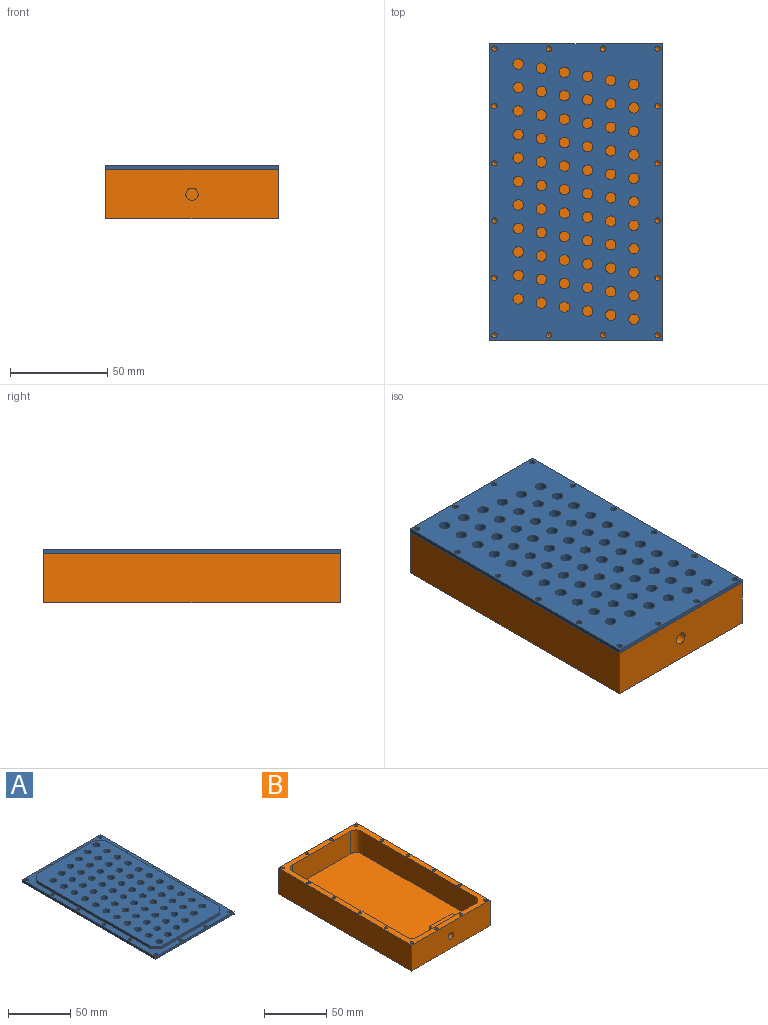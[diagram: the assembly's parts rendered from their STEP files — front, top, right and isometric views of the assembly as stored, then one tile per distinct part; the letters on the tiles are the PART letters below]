
ASSEMBLY  parts=2 mates=1
PART A: 97 faces, bbox 88.9x152.4x4.8 mm
  f0: cylinder r=1.39mm len=2.78mm, axis (0,0,1), area 20mm2, adj f19,f90
  f1: cylinder r=1.39mm len=2.78mm, axis (0,0,1), area 20mm2, adj f19,f90
  f2: cylinder r=1.39mm len=2.78mm, axis (0,0,1), area 20mm2, adj f19,f90
  f3: cylinder r=1.39mm len=2.78mm, axis (0,0,1), area 20mm2, adj f19,f90
  f4: cylinder r=1.39mm len=2.78mm, axis (0,0,1), area 20mm2, adj f19,f90
  f5: cylinder r=1.39mm len=2.78mm, axis (0,0,1), area 20mm2, adj f19,f90
  f6: cylinder r=1.39mm len=2.78mm, axis (0,0,1), area 20mm2, adj f19,f90
  f7: cylinder r=1.39mm len=2.78mm, axis (0,0,1), area 20mm2, adj f19,f90
  f8: cylinder r=1.39mm len=2.78mm, axis (0,0,1), area 20mm2, adj f19,f90
  f9: cylinder r=1.39mm len=2.78mm, axis (0,0,1), area 20mm2, adj f19,f90
  f10: cylinder r=1.39mm len=2.78mm, axis (0,0,1), area 20mm2, adj f19,f90
  f11: cylinder r=1.39mm len=2.78mm, axis (0,0,1), area 20mm2, adj f19,f90
  f12: cylinder r=1.39mm len=2.78mm, axis (0,0,1), area 20mm2, adj f19,f90
  f13: cylinder r=1.39mm len=2.78mm, axis (0,0,1), area 20mm2, adj f19,f90
  f14: plane 152.4x2.29mm, normal (1,0,0), area 348.4mm2, adj f17,f18,f19,f90
  f15: plane 142.24x78.74mm, normal (0,0,1), area 9602.1mm2, adj f20,f21,f22,f23,f24,f25,f26,f27
  f16: plane 152.4x2.29mm, normal (-1,0,0), area 348.4mm2, adj f17,f18,f19,f90
  f17: plane 88.9x2.29mm, normal (0,-1,0), area 203.2mm2, adj f14,f16,f19,f90
  f18: plane 88.9x2.29mm, normal (0,1,0), area 203.2mm2, adj f14,f16,f19,f90
  f19: plane 152.4x88.9mm, normal (0,0,-1), area 11934.1mm2, adj f0,f1,f2,f3,f4,f5,f6,f7
  f20: cylinder r=2.71mm len=5.41mm, axis (0,0,-1), area 82mm2, adj f15,f19
  f21: cylinder r=2.71mm len=5.41mm, axis (0,0,-1), area 82mm2, adj f15,f19
  f22: cylinder r=2.71mm len=5.41mm, axis (0,0,-1), area 82mm2, adj f15,f19
  f23: cylinder r=2.71mm len=5.41mm, axis (0,0,-1), area 82mm2, adj f15,f19
  f24: cylinder r=2.71mm len=5.41mm, axis (0,0,-1), area 82mm2, adj f15,f19
  f25: cylinder r=2.71mm len=5.41mm, axis (0,0,-1), area 82mm2, adj f15,f19
  f26: cylinder r=2.71mm len=5.41mm, axis (0,0,-1), area 82mm2, adj f15,f19
  f27: cylinder r=2.71mm len=5.41mm, axis (0,0,-1), area 82mm2, adj f15,f19
  f28: cylinder r=2.71mm len=5.41mm, axis (0,0,-1), area 82mm2, adj f15,f19
  f29: cylinder r=2.71mm len=5.41mm, axis (0,0,-1), area 82mm2, adj f15,f19
  f30: cylinder r=2.71mm len=5.41mm, axis (0,0,-1), area 82mm2, adj f15,f19
  f31: cylinder r=2.71mm len=5.41mm, axis (0,0,-1), area 82mm2, adj f15,f19
  f32: cylinder r=2.71mm len=5.41mm, axis (0,0,-1), area 82mm2, adj f15,f19
  f33: cylinder r=2.71mm len=5.41mm, axis (0,0,-1), area 82mm2, adj f15,f19
  f34: cylinder r=2.71mm len=5.41mm, axis (0,0,-1), area 82mm2, adj f15,f19
  f35: cylinder r=2.71mm len=5.41mm, axis (0,0,-1), area 82mm2, adj f15,f19
  f36: cylinder r=2.71mm len=5.41mm, axis (0,0,-1), area 82mm2, adj f15,f19
  f37: cylinder r=2.71mm len=5.41mm, axis (0,0,-1), area 82mm2, adj f15,f19
  f38: cylinder r=2.71mm len=5.41mm, axis (0,0,-1), area 82mm2, adj f15,f19
  f39: cylinder r=2.71mm len=5.41mm, axis (0,0,-1), area 82mm2, adj f15,f19
  f40: cylinder r=2.71mm len=5.41mm, axis (0,0,-1), area 82mm2, adj f15,f19
  f41: cylinder r=2.71mm len=5.41mm, axis (0,0,-1), area 82mm2, adj f15,f19
  f42: cylinder r=2.71mm len=5.41mm, axis (0,0,-1), area 82mm2, adj f15,f19
  f43: cylinder r=2.71mm len=5.41mm, axis (0,0,-1), area 82mm2, adj f15,f19
  f44: cylinder r=2.71mm len=5.41mm, axis (0,0,-1), area 82mm2, adj f15,f19
  f45: cylinder r=2.71mm len=5.41mm, axis (0,0,-1), area 82mm2, adj f15,f19
  f46: cylinder r=2.71mm len=5.41mm, axis (0,0,-1), area 82mm2, adj f15,f19
  f47: cylinder r=2.71mm len=5.41mm, axis (0,0,-1), area 82mm2, adj f15,f19
  f48: cylinder r=2.71mm len=5.41mm, axis (0,0,-1), area 82mm2, adj f15,f19
  f49: cylinder r=2.71mm len=5.41mm, axis (0,0,-1), area 82mm2, adj f15,f19
  f50: cylinder r=2.71mm len=5.41mm, axis (0,0,-1), area 82mm2, adj f15,f19
  f51: cylinder r=2.71mm len=5.41mm, axis (0,0,-1), area 82mm2, adj f15,f19
  f52: cylinder r=2.71mm len=5.41mm, axis (0,0,-1), area 82mm2, adj f15,f19
  f53: cylinder r=2.71mm len=5.41mm, axis (0,0,-1), area 82mm2, adj f15,f19
  f54: cylinder r=2.71mm len=5.41mm, axis (0,0,-1), area 82mm2, adj f15,f19
  f55: cylinder r=2.71mm len=5.41mm, axis (0,0,-1), area 82mm2, adj f15,f19
  f56: cylinder r=2.71mm len=5.41mm, axis (0,0,-1), area 82mm2, adj f15,f19
  f57: cylinder r=2.71mm len=5.41mm, axis (0,0,-1), area 82mm2, adj f15,f19
  f58: cylinder r=2.71mm len=5.41mm, axis (0,0,-1), area 82mm2, adj f15,f19
  f59: cylinder r=2.71mm len=5.41mm, axis (0,0,-1), area 82mm2, adj f15,f19
  f60: cylinder r=2.71mm len=5.41mm, axis (0,0,-1), area 82mm2, adj f15,f19
  f61: cylinder r=2.71mm len=5.41mm, axis (0,0,-1), area 82mm2, adj f15,f19
  f62: cylinder r=2.71mm len=5.41mm, axis (0,0,-1), area 82mm2, adj f15,f19
  f63: cylinder r=2.71mm len=5.41mm, axis (0,0,-1), area 82mm2, adj f15,f19
  f64: cylinder r=2.71mm len=5.41mm, axis (0,0,-1), area 82mm2, adj f15,f19
  f65: cylinder r=2.71mm len=5.41mm, axis (0,0,-1), area 82mm2, adj f15,f19
  f66: cylinder r=2.71mm len=5.41mm, axis (0,0,-1), area 82mm2, adj f15,f19
  f67: cylinder r=2.71mm len=5.41mm, axis (0,0,-1), area 82mm2, adj f15,f19
  f68: cylinder r=2.71mm len=5.41mm, axis (0,0,-1), area 82mm2, adj f15,f19
  f69: cylinder r=2.71mm len=5.41mm, axis (0,0,-1), area 82mm2, adj f15,f19
  f70: cylinder r=2.71mm len=5.41mm, axis (0,0,-1), area 82mm2, adj f15,f19
  f71: cylinder r=2.71mm len=5.41mm, axis (0,0,-1), area 82mm2, adj f15,f19
  f72: cylinder r=2.71mm len=5.41mm, axis (0,0,-1), area 82mm2, adj f15,f19
  f73: cylinder r=2.71mm len=5.41mm, axis (0,0,-1), area 82mm2, adj f15,f19
  f74: cylinder r=2.71mm len=5.41mm, axis (0,0,-1), area 82mm2, adj f15,f19
  f75: cylinder r=2.71mm len=5.41mm, axis (0,0,-1), area 82mm2, adj f15,f19
  f76: cylinder r=2.71mm len=5.41mm, axis (0,0,-1), area 82mm2, adj f15,f19
  f77: cylinder r=2.71mm len=5.41mm, axis (0,0,-1), area 82mm2, adj f15,f19
  f78: cylinder r=2.71mm len=5.41mm, axis (0,0,-1), area 82mm2, adj f15,f19
  f79: cylinder r=2.71mm len=5.41mm, axis (0,0,-1), area 82mm2, adj f15,f19
  f80: cylinder r=2.71mm len=5.41mm, axis (0,0,-1), area 82mm2, adj f15,f19
  f81: cylinder r=2.71mm len=5.41mm, axis (0,0,-1), area 82mm2, adj f15,f19
  f82: cylinder r=2.71mm len=5.41mm, axis (0,0,-1), area 82mm2, adj f15,f19
  f83: cylinder r=2.71mm len=5.41mm, axis (0,0,-1), area 82mm2, adj f15,f19
  f84: cylinder r=2.71mm len=5.41mm, axis (0,0,-1), area 82mm2, adj f15,f19
  f85: cylinder r=2.71mm len=5.41mm, axis (0,0,-1), area 82mm2, adj f15,f19
  f86: plane 129.54x2.54mm, normal (-1,0,0), area 329mm2, adj f15,f90,f91,f94
  f87: plane 66.04x2.54mm, normal (0,1,0), area 167.7mm2, adj f15,f90,f91,f92
  f88: plane 129.54x2.54mm, normal (1,0,0), area 329mm2, adj f15,f90,f92,f93
  f89: plane 66.04x2.54mm, normal (0,-1,0), area 167.7mm2, adj f15,f90,f93,f94
  f90: plane 152.4x88.9mm, normal (0,0,1), area 2332mm2, adj f0,f1,f2,f3,f4,f5,f6,f7
  f91: plane 6.35x6.35mm, normal (-0.71,0.71,0), area 22.8mm2, adj f15,f86,f87,f90
  f92: plane 6.35x6.35mm, normal (0.71,0.71,0), area 22.8mm2, adj f15,f87,f88,f90
  f93: plane 6.35x6.35mm, normal (0.71,-0.71,0), area 22.8mm2, adj f15,f88,f89,f90
  f94: plane 6.35x6.35mm, normal (-0.71,-0.71,0), area 22.8mm2, adj f15,f86,f89,f90
  f95: cylinder r=1.39mm len=2.78mm, axis (0,0,1), area 20mm2, adj f19,f90
  f96: cylinder r=1.39mm len=2.78mm, axis (0,0,1), area 20mm2, adj f19,f90
PART B: 64 faces, bbox 88.9x152.4x25.4 mm
  f0: plane 25.4x19.18mm, normal (0,1,0), area 455.4mm2, adj f1,f2,f27,f62,f63
  f1: cylinder r=6.35mm len=19.18mm, axis (0,0,1), area 191.3mm2, adj f0,f23,f27,f63
  f2: cylinder r=6.35mm len=19.18mm, axis (0,0,-1), area 191.3mm2, adj f0,f23,f27,f63
  f3: cone r=0mm half-angle=59deg, axis (0,0,1), area 6.7mm2, adj f4
  f4: cylinder r=1.35mm len=11.91mm, axis (0,0,1), area 101.2mm2, adj f3,f17
  f5: cone r=0mm half-angle=59deg, axis (0,0,1), area 6.7mm2, adj f6
  f6: cylinder r=1.35mm len=11.91mm, axis (0,0,1), area 101.2mm2, adj f5,f17
  f7: cone r=0mm half-angle=59deg, axis (0,0,1), area 6.7mm2, adj f8
  f8: cylinder r=1.35mm len=11.91mm, axis (0,0,1), area 101.2mm2, adj f7,f17
  f9: cone r=0mm half-angle=59deg, axis (0,0,1), area 6.7mm2, adj f10
  f10: cylinder r=1.35mm len=11.91mm, axis (0,0,1), area 101.2mm2, adj f9,f17
  f11: cone r=0mm half-angle=59deg, axis (0,0,1), area 6.7mm2, adj f12
  f12: cylinder r=1.35mm len=11.91mm, axis (0,0,1), area 101.2mm2, adj f11,f17
  f13: cone r=0mm half-angle=59deg, axis (0,0,1), area 6.7mm2, adj f14
  f14: cylinder r=1.35mm len=11.91mm, axis (0,0,1), area 101.2mm2, adj f13,f17
  f15: cone r=0mm half-angle=59deg, axis (0,0,1), area 6.7mm2, adj f16
  f16: cylinder r=1.35mm len=11.91mm, axis (0,0,1), area 101.2mm2, adj f15,f17
  f17: plane 152.4x88.9mm, normal (0,0,1), area 2291mm2, adj f4,f6,f8,f10,f12,f14,f16,f18
  f18: plane 152.4x25.4mm, normal (1,0,0), area 3871mm2, adj f17,f19,f21,f22
  f19: plane 88.9x25.4mm, normal (0,1,0), area 2258.1mm2, adj f17,f18,f20,f22
  f20: plane 152.4x25.4mm, normal (-1,0,0), area 3871mm2, adj f17,f19,f21,f22
  f21: plane 88.9x25.4mm, normal (0,-1,0), area 2226.4mm2, adj f17,f18,f20,f22,f62
  f22: plane 152.4x88.9mm, normal (0,0,-1), area 13513.9mm2, adj f18,f19,f20,f21,f51,f53,f55,f57
  f23: plane 66.04x22.23mm, normal (0,1,0), area 737.1mm2, adj f1,f2,f17,f27,f28,f31,f63
  f24: plane 129.54x22.23mm, normal (-1,0,0), area 2879mm2, adj f17,f27,f28,f29
  f25: plane 66.04x22.23mm, normal (0,-1,0), area 1467.7mm2, adj f17,f27,f29,f30
  f26: plane 129.54x22.23mm, normal (1,0,0), area 2879mm2, adj f17,f27,f30,f31
  f27: plane 142.24x78.74mm, normal (0,0,1), area 10986.8mm2, adj f0,f1,f2,f23,f24,f25,f26,f28
  f28: cylinder r=6.35mm len=22.23mm, axis (0,0,1), area 221.7mm2, adj f17,f23,f24,f27
  f29: cylinder r=6.35mm len=22.23mm, axis (0,0,-1), area 221.7mm2, adj f17,f24,f25,f27
  f30: cylinder r=6.35mm len=22.23mm, axis (0,0,1), area 221.7mm2, adj f17,f25,f26,f27
  f31: cylinder r=6.35mm len=22.23mm, axis (0,0,-1), area 221.7mm2, adj f17,f23,f26,f27
  f32: cone r=0mm half-angle=59deg, axis (0,0,1), area 6.7mm2, adj f33
  f33: cylinder r=1.35mm len=11.91mm, axis (0,0,1), area 101.2mm2, adj f17,f32
  f34: cone r=0mm half-angle=59deg, axis (0,0,1), area 6.7mm2, adj f35
  f35: cylinder r=1.35mm len=11.91mm, axis (0,0,1), area 101.2mm2, adj f17,f34
  f36: cone r=0mm half-angle=59deg, axis (0,0,1), area 6.7mm2, adj f37
  f37: cylinder r=1.35mm len=11.91mm, axis (0,0,1), area 101.2mm2, adj f17,f36
  f38: cone r=0mm half-angle=59deg, axis (0,0,1), area 6.7mm2, adj f39
  f39: cylinder r=1.35mm len=11.91mm, axis (0,0,1), area 101.2mm2, adj f17,f38
  f40: cone r=0mm half-angle=59deg, axis (0,0,1), area 6.7mm2, adj f41
  f41: cylinder r=1.35mm len=11.91mm, axis (0,0,1), area 101.2mm2, adj f17,f40
  f42: cone r=0mm half-angle=59deg, axis (0,0,1), area 6.7mm2, adj f43
  f43: cylinder r=1.35mm len=11.91mm, axis (0,0,1), area 101.2mm2, adj f17,f42
  f44: cone r=0mm half-angle=59deg, axis (0,0,1), area 6.7mm2, adj f45
  f45: cylinder r=1.35mm len=11.91mm, axis (0,0,1), area 101.2mm2, adj f17,f44
  f46: cone r=0mm half-angle=59deg, axis (0,0,1), area 6.7mm2, adj f47
  f47: cylinder r=1.35mm len=11.91mm, axis (0,0,1), area 101.2mm2, adj f17,f46
  f48: cone r=0mm half-angle=59deg, axis (0,0,1), area 6.7mm2, adj f49
  f49: cylinder r=1.35mm len=11.91mm, axis (0,0,1), area 101.2mm2, adj f17,f48
  f50: cone r=0mm half-angle=59deg, axis (0,0,-1), area 6.7mm2, adj f51
  f51: cylinder r=1.35mm len=11.91mm, axis (0,0,-1), area 101.2mm2, adj f22,f50
  f52: cone r=0mm half-angle=59deg, axis (0,0,-1), area 6.7mm2, adj f53
  f53: cylinder r=1.35mm len=11.91mm, axis (0,0,-1), area 101.2mm2, adj f22,f52
  f54: cone r=0mm half-angle=59deg, axis (0,0,-1), area 6.7mm2, adj f55
  f55: cylinder r=1.35mm len=11.91mm, axis (0,0,-1), area 101.2mm2, adj f22,f54
  f56: cone r=0mm half-angle=59deg, axis (0,0,-1), area 6.7mm2, adj f57
  f57: cylinder r=1.35mm len=11.91mm, axis (0,0,-1), area 101.2mm2, adj f22,f56
  f58: cone r=0mm half-angle=59deg, axis (0,0,-1), area 6.7mm2, adj f59
  f59: cylinder r=1.35mm len=11.91mm, axis (0,0,-1), area 101.2mm2, adj f22,f58
  f60: cone r=0mm half-angle=59deg, axis (0,0,-1), area 6.7mm2, adj f61
  f61: cylinder r=1.35mm len=11.91mm, axis (0,0,-1), area 101.2mm2, adj f22,f60
  f62: cylinder r=3.17mm len=11.43mm, axis (0,-1,0), area 228mm2, adj f0,f21
  f63: plane 38.1x6.35mm, normal (0,0,1), area 178.6mm2, adj f0,f1,f2,f23
PLACE A rot(axis=(0,1,0),180deg) t=(-0.09,-6.62,14.28)mm
PLACE B t=(-0.09,-1.54,-8.58)mm fixed
MATE fastened B.f17 <-> A.f90  axis (0,0,1) through (44.36,-77.74,16.82)mm
